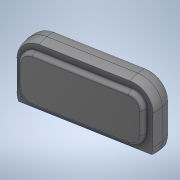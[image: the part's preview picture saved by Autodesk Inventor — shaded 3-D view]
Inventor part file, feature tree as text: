
AUTODESK INVENTOR PART (.ipt)
format: ipt  version: 2022 (Build 260153000, 153)  size: 1,125,376 bytes
history: mixed  units: mm
features: other x6, extrude x1, sketch x1, imported_body x1
ambient origin geometry x8: Origin, YZ Plane, XZ Plane, XY Plane, X Axis, Y Axis, Z Axis, Center Point
bodies: Body1 (imported_parasolid), Body2 (imported_parasolid), Body3 (imported_parasolid)
feature tree (9):
  extrude  "Выдавливание1"  Depth=1.25mm TaperAngle=0.0deg
  other  "Твердое тело2"
  other  "Твердое тело3"
  other  "Твердое тело4"
  sketch  "Эскиз1"
  other  "Hoofdunit-1-solid1"
  other  "Hoofdunit-1-solid2"
  other  "Hoofdunit-1-solid3"
  imported_body  NMx_Import_Brep_tag  [imported B-rep: ~18 faces, bbox_mm=[28.762576, 13.6, 5.607055]]
